# Revit family: Control_Unit-Lutron-Energi_Savr_Node-QSN-4T5-120-D
name_source: partatom
category: Lighting Devices
revit_build: Autodesk Revit 2018 (Build: 20170223_1515(x64)
units: mm (PartAtom-declared; Revit-internal decimal feet)

## family parameters
Cut with Voids When Loaded = No
Host = Face
Maintain Annotation Orientation = Yes
OmniClass Number = 23.80.30.11.17
OmniClass Title = Distribution Boards and Control Panels
Part Type = Normal
Room Calculation Point = No
Round Connector Dimension = Use Radius
Shared = No

## types (1)
- QSN-4T5-120-D
    Assembly Code = D3060
    Cost = 0 $
    Current = 5 A
    Default Elevation = 48 "
    Description = The Energi Savr Node (ESN) family is a group of modular products for the control of lighting loads.
    Finish = Plastic - Lutron - White - Matte
    Frequency = 50|60 Hz
    Instruction Sheet Link = http://www.lutron.com
    Manufacturer = Lutron Electronics Co., Inc
    Manufacturer Fax Number = 610-282-1243
    Maximum Operating Temperature = 104 °F
    Minimum Operating Temperature = 32 °F
    Model = Athena
    Number of Poles = 1
    Operating Voltage = 120 V~ 50/60 Hz 5 A of switching load per zone | 16 A maximum per module
    Overall Depth = 3.53 "
    Overall Height = 2.38 "
    Overall Width = 6.37 "
    Performance URL = http://www.lutron.com
    Product Documentation Link = https://www.lutron.com
    Product Name = 0–10 V- Power Module
    Product Page URL = https://www.lutron.com
    Series = Energi Savr Node
    URL = http://www.lutron.com
    Version = 2018 - v1.0a
    Video Link = https://www.youtube.com
    Voltage = 120 V
    Warranty URL = http://www.lutron.com

## geometry (parser evidence)
native form markers: Sweep x3
no freeform markers — native parametric forms only
